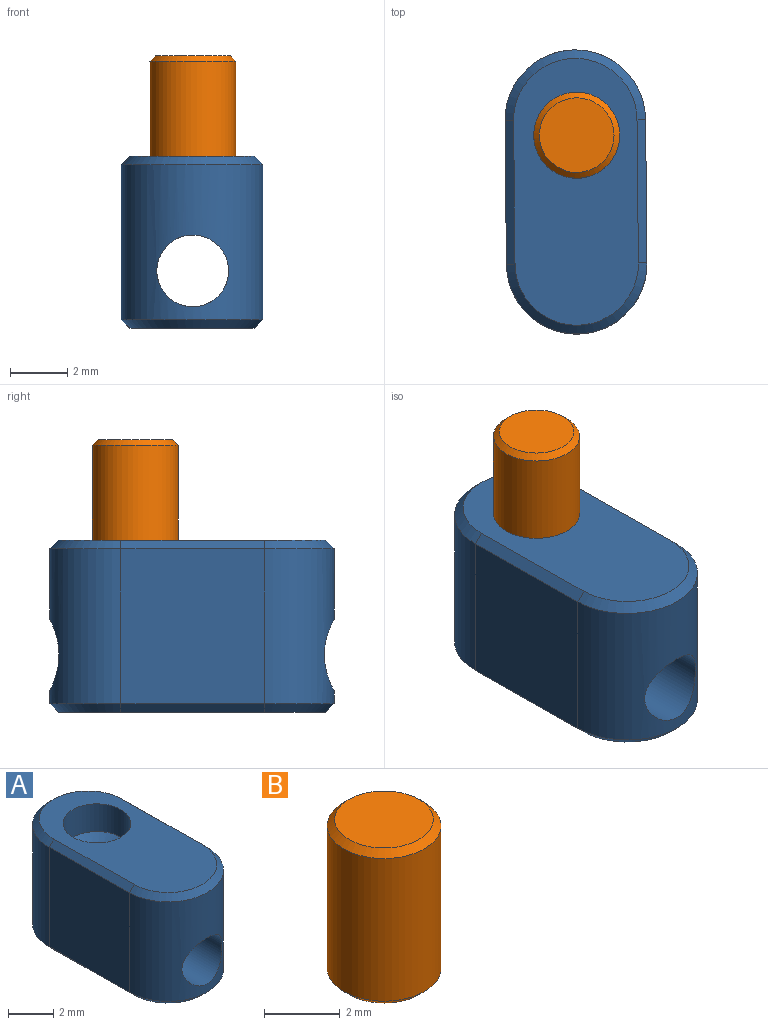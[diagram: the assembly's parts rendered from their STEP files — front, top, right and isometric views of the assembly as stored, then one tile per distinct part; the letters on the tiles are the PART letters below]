
ASSEMBLY  parts=2 mates=1
PART A: 17 faces, bbox 4.9x9.9x6 mm
  f0: cylinder r=2.45mm len=5.4mm, axis (0,0,1), area 36.5mm2, adj f2,f3,f10,f14,f16
  f1: cylinder r=2.45mm len=5.4mm, axis (0,0,1), area 36.5mm2, adj f2,f3,f9,f13,f16
  f2: plane 5.4x5mm, normal (1,0.01,0), area 27mm2, adj f0,f1,f8,f12
  f3: plane 5.4x5mm, normal (-1,-0.01,0), area 27mm2, adj f0,f1,f11,f15
  f4: plane 9.3x4.35mm, normal (0,0,-1), area 36mm2, adj f8,f9,f10,f11
  f5: plane 9.3x4.35mm, normal (0,0,1), area 29mm2, adj f7,f12,f13,f14,f15
  f6: cone r=0mm half-angle=59deg, axis (0,0,1), area 8.2mm2, adj f7
  f7: cylinder r=1.5mm len=3mm, axis (0,0,1), area 14.1mm2, adj f5,f6
  f8: plane 5x0.35mm, normal (0.71,0.01,-0.71), area 2.1mm2, adj f2,f4,f9,f10
  f9: cone r=2.15mm half-angle=45deg, axis (0,0,1), area 3.1mm2, adj f1,f4,f8,f11
  f10: cone r=2.15mm half-angle=45deg, axis (0,0,1), area 3.1mm2, adj f0,f4,f8,f11
  f11: plane 5x0.35mm, normal (-0.71,-0.01,-0.71), area 2.1mm2, adj f3,f4,f9,f10
  f12: plane 5x0.35mm, normal (0.71,0.01,0.71), area 2.1mm2, adj f2,f5,f13,f14
  f13: cone r=2.45mm half-angle=45deg, axis (0,0,-1), area 3.1mm2, adj f1,f5,f12,f15
  f14: cone r=2.45mm half-angle=45deg, axis (0,0,-1), area 3.1mm2, adj f0,f5,f12,f15
  f15: plane 5x0.35mm, normal (-0.71,-0.01,0.71), area 2.1mm2, adj f3,f5,f13,f14
  f16: cylinder r=1.25mm len=9.9mm, axis (0,1,0), area 75.1mm2, adj f0,f1
PART B: 5 faces, bbox 3x3x5 mm
  f0: cylinder r=1.5mm len=4.6mm, axis (0,0,-1), area 43.4mm2, adj f3,f4
  f1: plane 2.6x2.6mm, normal (0,0,1), area 5.3mm2, adj f4
  f2: plane 2.6x2.6mm, normal (0,0,-1), area 5.3mm2, adj f3
  f3: cone r=1.5mm half-angle=45deg, axis (0,0,1), area 2.5mm2, adj f0,f2
  f4: cone r=1.3mm half-angle=45deg, axis (0,0,-1), area 2.5mm2, adj f0,f1
PLACE A t=(-6.33,-77.24,-19)mm
PLACE B t=(-6.33,-77.24,-18.5)mm
MATE fastened A.f6 <-> B.f0  axis (0,0,1) through (0.02,1.97,4.5)mm
